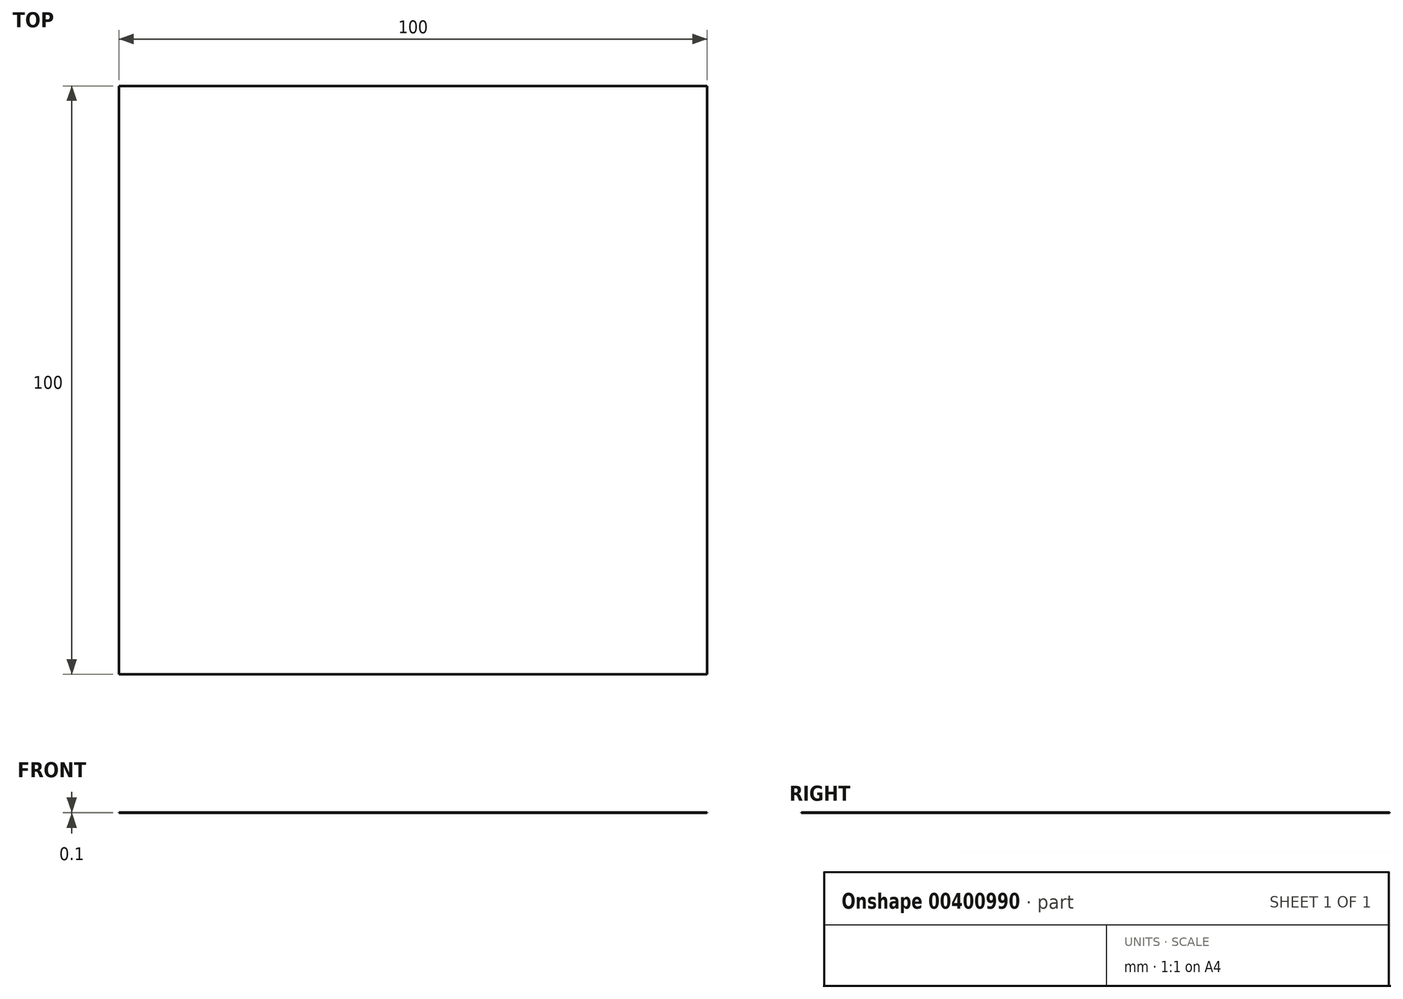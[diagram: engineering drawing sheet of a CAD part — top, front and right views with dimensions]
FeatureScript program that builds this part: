
annotation { "Feature Type Name" : "Feature", "Feature Type Description" : "" }
export const myFeature = defineFeature(function(context is Context, id is Id, definition is map)
    precondition{}
    {
        {
            var Q0;
            Q0=qCreatedBy(makeId("Top.planeOp"),FACE);
            var sketch = newSketch(context, id + "F0", { "sketchPlane" : qUnion([Q0])});
            skLineSegment(sketch, "E0.bottom", {"start": v(50, 50) * mm, "end": v(-50, 50) * mm});
            skLineSegment(sketch, "E0.top", {"start": v(50, -50) * mm, "end": v(-50, -50) * mm});
            skLineSegment(sketch, "E0.left", {"start": v(50, 50) * mm, "end": v(50, -50) * mm});
            skLineSegment(sketch, "E0.right", {"start": v(-50, 50) * mm, "end": v(-50, -50) * mm});
            skPoint(sketch, "E0.middle", {"position": v(0, 0) * mm});
            skLineSegment(sketch, "E1", {"start": v(0, 0) * mm, "end": v(-16.44, 0) * mm});
            skLineSegment(sketch, "E2", {"start": v(-16.44, 0) * mm, "end": v(17.56, 0) * mm});
            skSolve(sketch);
        }
        {
            var Q0;
            Q0=makeQuery(id+"F0.imprint","IMPRINT",FACE,{"disambiguationData":[TD([[makeQuery(id+"F0.imprint","IMPRINT",EDGE,{"derivedFrom":sQuery(id+"F0.wireOp",EDGE,"E0.bottom")}),1.0]])]});
            extrude(context, id + "F1", {"entities" : qUnion([Q0]), "depth" : 0.1 * mm});
        }
    });
